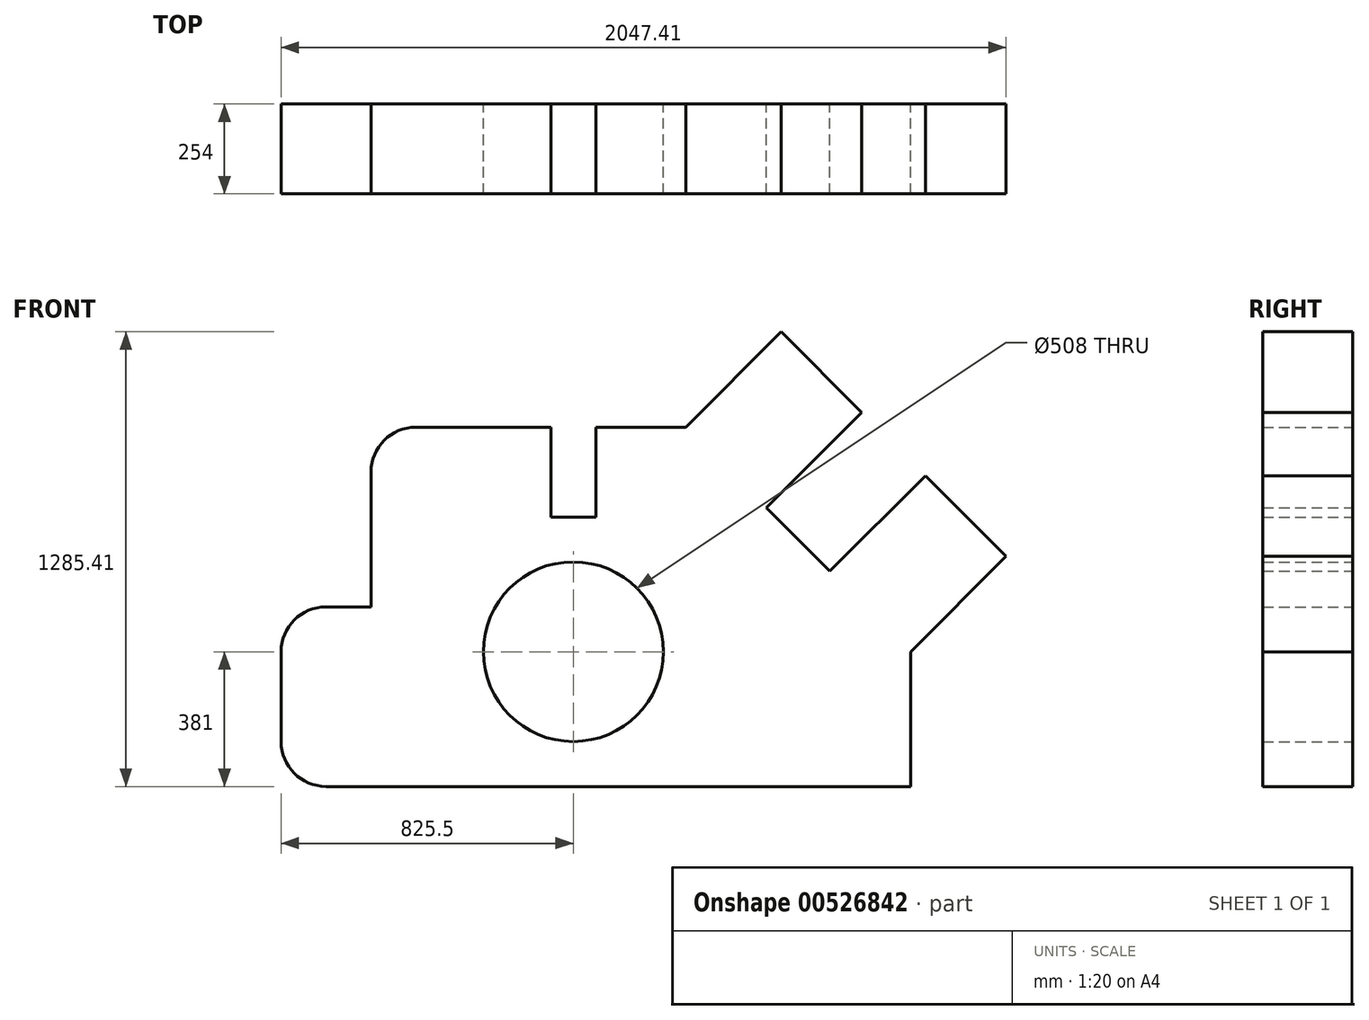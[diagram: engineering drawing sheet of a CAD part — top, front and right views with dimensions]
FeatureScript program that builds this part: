
annotation { "Feature Type Name" : "Feature", "Feature Type Description" : "" }
export const myFeature = defineFeature(function(context is Context, id is Id, definition is map)
    precondition{}
    {
        {
            var Q0;
            Q0=qCreatedBy(makeId("Front.planeOp"),FACE);
            var sketch = newSketch(context, id + "F0", { "sketchPlane" : qUnion([Q0])});
            skLineSegment(sketch, "E0", {"start": v(127, 0) * mm, "end": v(1778, 0) * mm});
            skLineSegment(sketch, "E1", {"start": v(1778, 0) * mm, "end": v(1778, 381) * mm});
            skPoint(sketch, "E2.visualSharp", {"position": v(0, 0) * mm});
            skCircle(sketch, "E3", {"center": v(825.5, 381) * mm, "radius": 254 * mm});
            skLineSegment(sketch, "E4", {"start": v(0, 127) * mm, "end": v(0, 381) * mm});
            skLineSegment(sketch, "E5", {"start": v(127, 508) * mm, "end": v(254, 508) * mm});
            skLineSegment(sketch, "E6", {"start": v(254, 508) * mm, "end": v(254, 889) * mm});
            skLineSegment(sketch, "E7", {"start": v(381, 1016) * mm, "end": v(762, 1016) * mm});
            skLineSegment(sketch, "E8", {"start": v(762, 1016) * mm, "end": v(762, 762) * mm});
            skLineSegment(sketch, "E9", {"start": v(762, 762) * mm, "end": v(889, 762) * mm});
            skLineSegment(sketch, "E10", {"start": v(889, 762) * mm, "end": v(889, 1016) * mm});
            skLineSegment(sketch, "E11", {"start": v(889, 1016) * mm, "end": v(1143, 1016) * mm});
            skLineSegment(sketch, "E12", {"start": v(1778, 381) * mm, "end": v(2047.4, 650.4) * mm});
            skLineSegment(sketch, "E13", {"start": v(2047.4, 650.4) * mm, "end": v(1819.71, 878.1) * mm});
            skLineSegment(sketch, "E14", {"start": v(1819.71, 878.1) * mm, "end": v(1550.3, 608.7) * mm});
            skLineSegment(sketch, "E15", {"start": v(1550.3, 608.7) * mm, "end": v(1370.7, 788.3) * mm});
            skLineSegment(sketch, "E16", {"start": v(1370.7, 788.3) * mm, "end": v(1640.1, 1057.71) * mm});
            skLineSegment(sketch, "E17", {"start": v(1640.1, 1057.71) * mm, "end": v(1412.4, 1285.4) * mm});
            skLineSegment(sketch, "E18", {"start": v(1412.4, 1285.4) * mm, "end": v(1143, 1016) * mm});
            skArc(sketch, "E19.filletArc", {"start": v(0, 127) * mm, "mid": v(37.2, 37.2) * mm, "end": v(127, 0) * mm});
            skPoint(sketch, "E20.visualSharp", {"position": v(0, 508) * mm});
            skArc(sketch, "E20.filletArc", {"start": v(127, 508) * mm, "mid": v(37.2, 470.8) * mm, "end": v(0, 381) * mm});
            skPoint(sketch, "E21.visualSharp", {"position": v(254, 1016) * mm});
            skArc(sketch, "E21.filletArc", {"start": v(381, 1016) * mm, "mid": v(291.2, 978.8) * mm, "end": v(254, 889) * mm});
            skSolve(sketch);
        }
        {
            var Q0;
            Q0=makeQuery(id+"F0.imprint","IMPRINT",FACE,{"disambiguationData":[TD([[makeQuery(id+"F0.imprint","IMPRINT",EDGE,{"derivedFrom":sQuery(id+"F0.wireOp",EDGE,"E0")}),1.0]])]});
            extrude(context, id + "F1", {"entities" : qUnion([Q0]), "depth" : 254 * mm, "offsetDistance" : 25.4 * mm});
        }
    });
